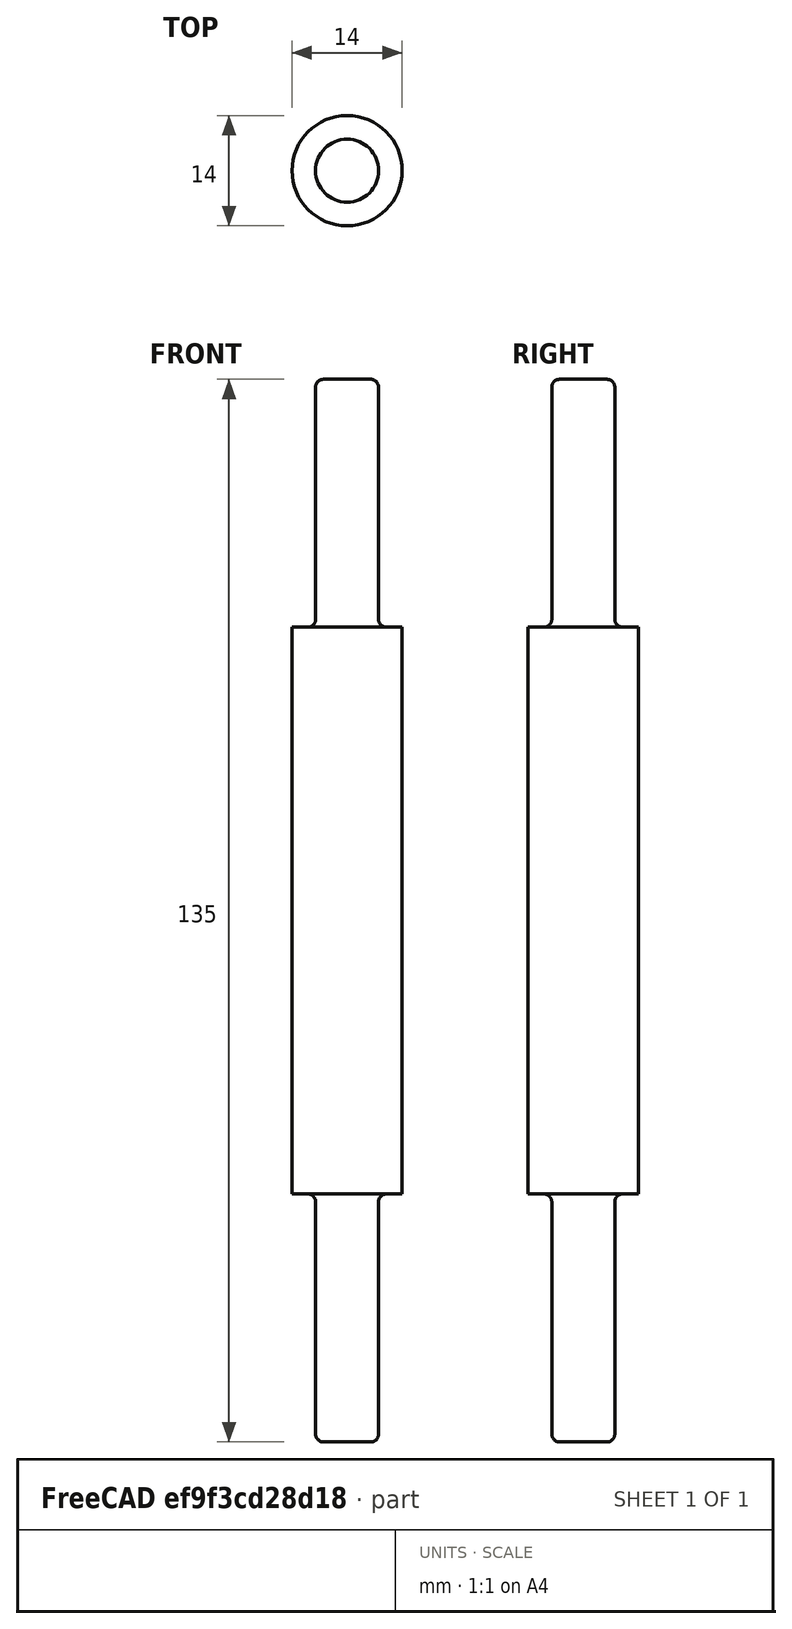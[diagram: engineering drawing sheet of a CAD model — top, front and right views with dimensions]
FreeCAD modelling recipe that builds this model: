
FCSTD DOCUMENT  (FreeCAD 0.21R33668 +7 (Git))
Label: FilamentHolderAxle
License: All rights reserved
LicenseURL: http://en.wikipedia.org/wiki/All_rights_reserved
objects: Part::Cylinder×2, PartDesign::FeatureBase×2, PartDesign::Fillet×2, Part::MultiFuse×1, PartDesign::Body×1, App::Part×1
note: 10 computed .brp shape members not serialized (recipe doc carries the construction recipe); baked Part::Feature solids carry a one-line shape summary decoded from their .brp

FEATURE [Part::Cylinder] Cylinder
  Angle = 360
  AttacherType = Attacher::AttachEngine3D
  FirstAngle = 0
  Height = 135
  Radius = 4
  SecondAngle = 0
FEATURE [PartDesign::FeatureBase] BaseFeature
  BaseFeature = -> Cylinder
FEATURE [PartDesign::Fillet] Fillet
  Base = -> BaseFeature [Face3,Face2]
  BaseFeature = -> BaseFeature
  Radius = 1
  SupportTransform = false
  UseAllEdges = false
FEATURE [Part::Cylinder] Cylinder001
  Angle = 360
  AttacherType = Attacher::AttachEngine3D
  FirstAngle = 0
  Height = 72
  Placement = pos=(0,0,31.5) rot=(0,0,1;0rad)
  Radius = 7
  SecondAngle = 0
  expr: .Placement.Base.z = (135 - 72) / 2
FEATURE [Part::MultiFuse] Fusion
  Shapes = -> [Cylinder001,Fillet]
FEATURE [PartDesign::FeatureBase] BaseFeature001
  BaseFeature = -> Fusion
FEATURE [PartDesign::Fillet] Fillet001
  Base = -> BaseFeature001 [Edge4,Edge5]
  BaseFeature = -> BaseFeature001
  Radius = 1
  SupportTransform = false
  UseAllEdges = false
FEATURE [PartDesign::Body] Body
  BaseFeature = -> Fusion
  Group = -> [BaseFeature001,Fillet001]
  Origin = -> Origin001
  Tip = -> Fillet001
FEATURE [App::Part] Part  label="FilamentHolderAxle"
  Group = -> [Cylinder,Body,Fillet,Cylinder001,BaseFeature,Fusion]
  Origin = -> Origin
